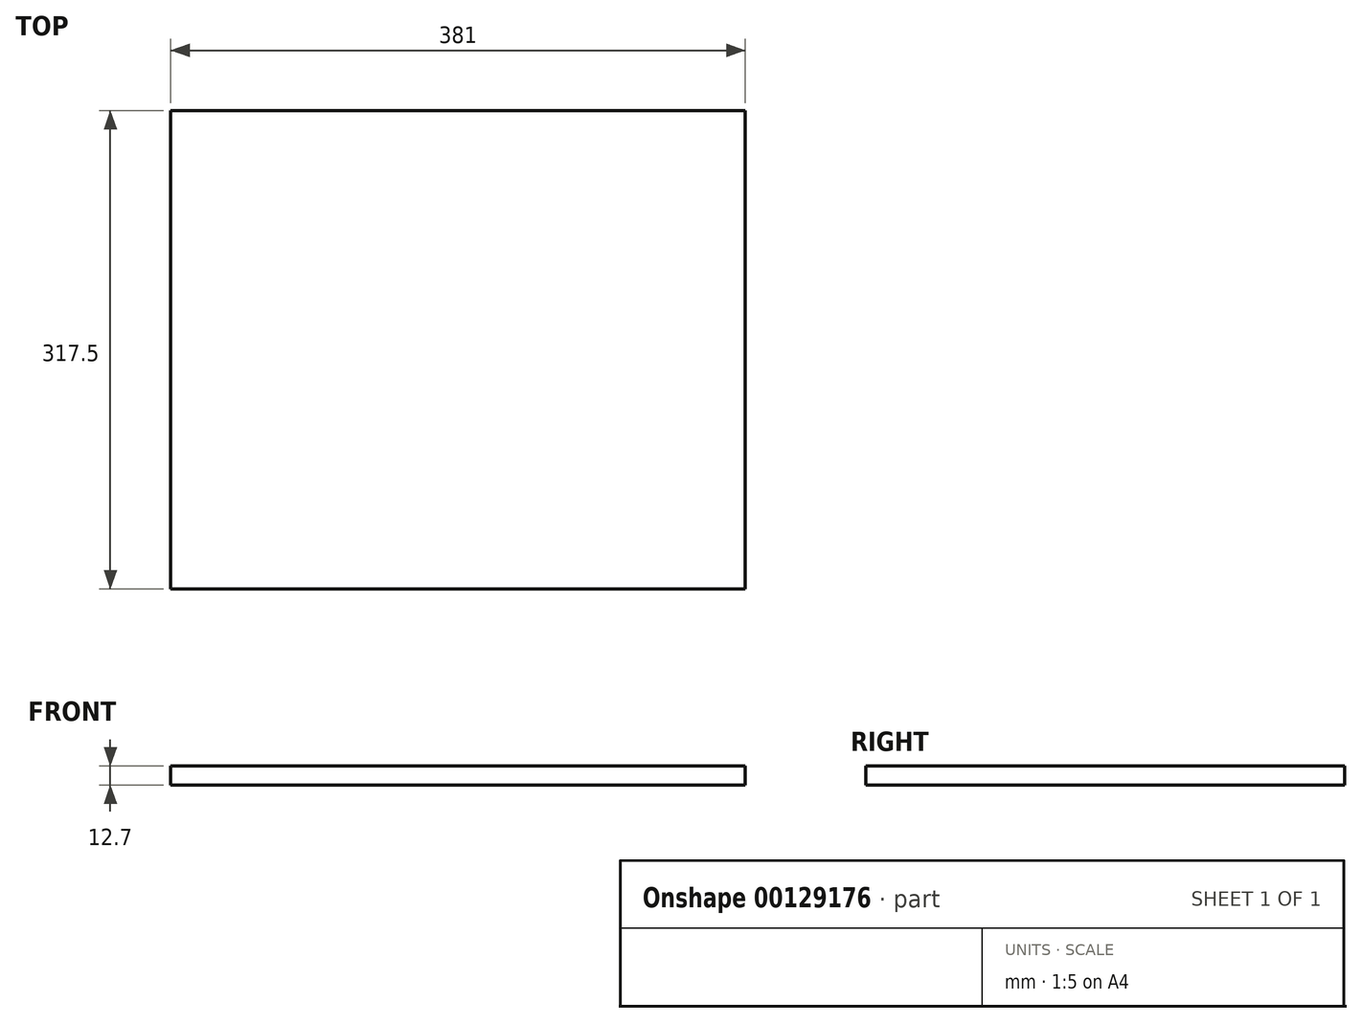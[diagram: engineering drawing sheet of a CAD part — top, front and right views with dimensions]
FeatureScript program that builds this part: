
annotation { "Feature Type Name" : "Feature", "Feature Type Description" : "" }
export const myFeature = defineFeature(function(context is Context, id is Id, definition is map)
    precondition{}
    {
        {
            var Q0;
            Q0=qCreatedBy(makeId("Top.planeOp"),FACE);
            var sketch = newSketch(context, id + "F0", { "sketchPlane" : qUnion([Q0])});
            skLineSegment(sketch, "E0.bottom", {"start": v(190.5, -158.75) * mm, "end": v(-190.5, -158.75) * mm});
            skLineSegment(sketch, "E0.top", {"start": v(190.5, 158.75) * mm, "end": v(-190.5, 158.75) * mm});
            skLineSegment(sketch, "E0.left", {"start": v(190.5, -158.75) * mm, "end": v(190.5, 158.75) * mm});
            skLineSegment(sketch, "E0.right", {"start": v(-190.5, -158.75) * mm, "end": v(-190.5, 158.75) * mm});
            skPoint(sketch, "E0.middle", {"position": v(0, 0) * mm});
            skSolve(sketch);
        }
        {
            var Q0;
            Q0 = qSketchRegion(id + "F0", true);
            extrude(context, id + "F1", {"entities" : qUnion([Q0]), "depth" : 12.7 * mm});
        }
    });
